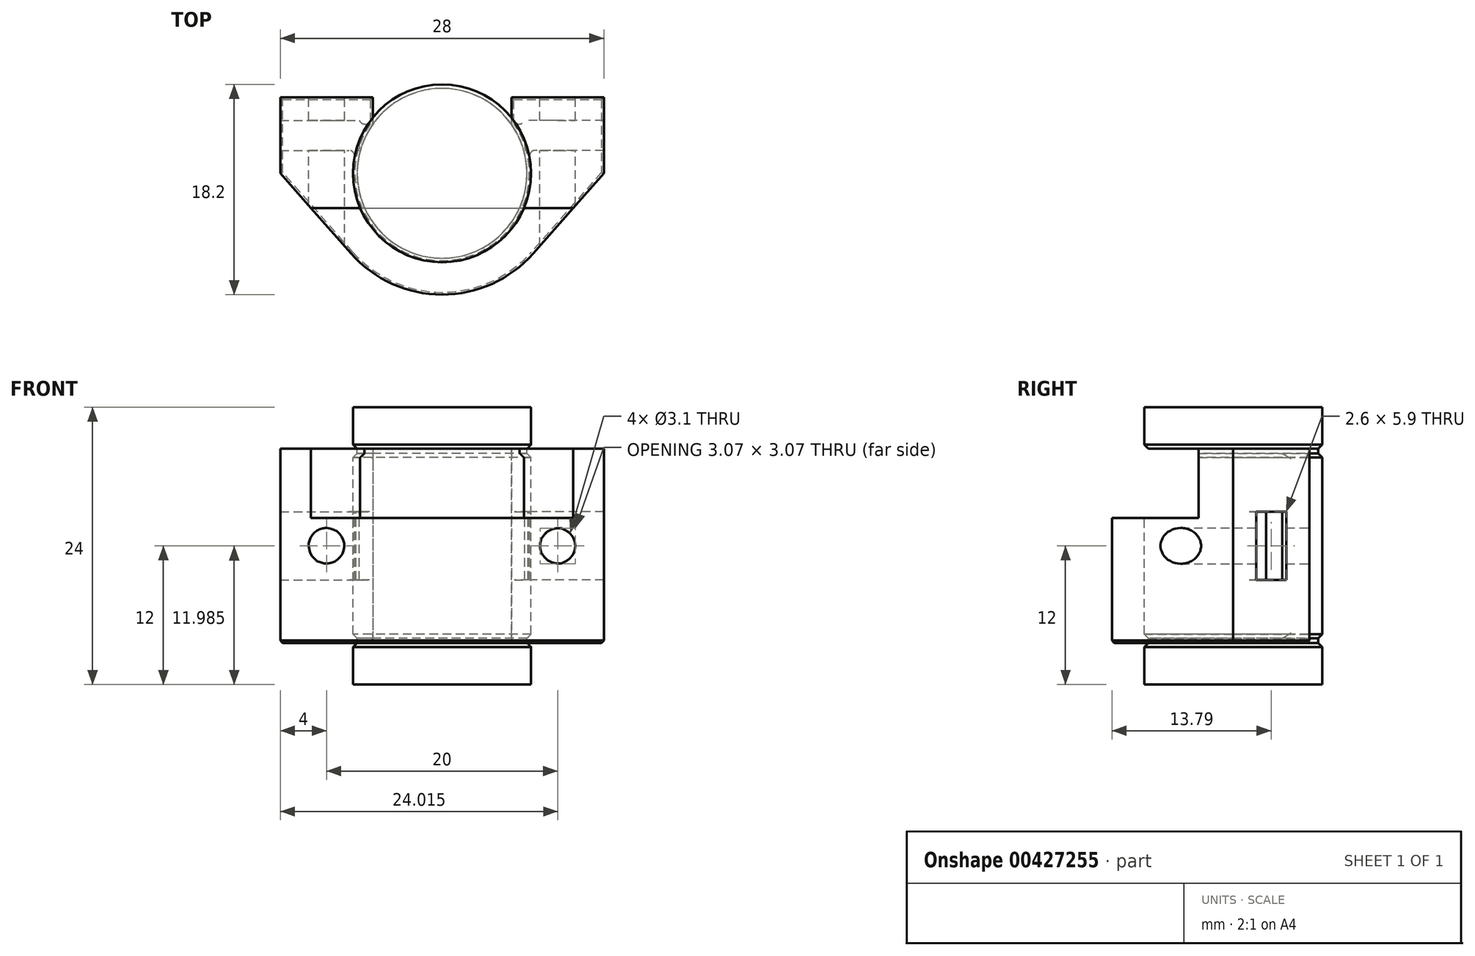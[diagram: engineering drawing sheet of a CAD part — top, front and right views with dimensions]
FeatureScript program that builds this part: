
annotation { "Feature Type Name" : "Feature", "Feature Type Description" : "" }
export const myFeature = defineFeature(function(context is Context, id is Id, definition is map)
    precondition{}
    {
        {
            var Q0;
            Q0=qCreatedBy(makeId("Front.planeOp"),FACE);
            var sketch = newSketch(context, id + "F0", { "sketchPlane" : qUnion([Q0])});
            skLineSegment(sketch, "E0", {"start": v(0, 12) * mm, "end": v(0, -12) * mm});
            skLineSegment(sketch, "E1.bottom", {"start": v(-4, 12) * mm, "end": v(-7.5, 12) * mm});
            skLineSegment(sketch, "E1.top", {"start": v(-4, -12) * mm, "end": v(-7.5, -12) * mm});
            skLineSegment(sketch, "E1.left", {"start": v(-4, 12) * mm, "end": v(-4, -12) * mm, "construction": true});
            skLineSegment(sketch, "E2", {"start": v(-7.5, 12) * mm, "end": v(-7.5, 8.75) * mm, "construction": true});
            skLineSegment(sketch, "E3", {"start": v(-7.5, 8.75) * mm, "end": v(-7.15, 8.75) * mm, "construction": true});
            skLineSegment(sketch, "E4", {"start": v(-7.15, 8.75) * mm, "end": v(-7.15, 7.65) * mm, "construction": true});
            skLineSegment(sketch, "E5", {"start": v(-7.15, 7.65) * mm, "end": v(-7.5, 7.65) * mm, "construction": true});
            skLineSegment(sketch, "E6", {"start": v(-7.5, 7.65) * mm, "end": v(-7.5, 0) * mm, "construction": true});
            skLineSegment(sketch, "E7.MirrorCS", {"start": v(-7.5, -8.75) * mm, "end": v(-7.15, -8.75) * mm, "construction": true});
            skLineSegment(sketch, "E8.MirrorCS", {"start": v(-7.15, -8.75) * mm, "end": v(-7.15, -7.65) * mm, "construction": true});
            skLineSegment(sketch, "E9.MirrorCS", {"start": v(-7.15, -7.65) * mm, "end": v(-7.5, -7.65) * mm, "construction": true});
            skLineSegment(sketch, "E10", {"start": v(-7.5, 0) * mm, "end": v(-7.5, -7.65) * mm, "construction": true});
            skLineSegment(sketch, "E11", {"start": v(-7.5, -8.75) * mm, "end": v(-7.5, -12) * mm, "construction": true});
            skLineSegment(sketch, "E12.0", {"start": v(-7.7, 12) * mm, "end": v(-7.7, 8.75) * mm});
            skLineSegment(sketch, "E13.0", {"start": v(-7.35, 8.75) * mm, "end": v(-7.35, 7.65) * mm});
            skLineSegment(sketch, "E14", {"start": v(-7.7, 8.75) * mm, "end": v(-7.35, 8.4) * mm});
            skLineSegment(sketch, "E15", {"start": v(-7.7, 7.65) * mm, "end": v(-7.7, 0) * mm});
            skLineSegment(sketch, "E16", {"start": v(-7.7, 7.65) * mm, "end": v(-7.35, 8) * mm});
            skLineSegment(sketch, "E17", {"start": v(-7.7, 12) * mm, "end": v(-7.5, 12) * mm});
            skLineSegment(sketch, "E18.MirrorCS", {"start": v(-7.7, -7.65) * mm, "end": v(-7.7, 0) * mm});
            skLineSegment(sketch, "E19.MirrorCS", {"start": v(-7.7, -7.65) * mm, "end": v(-7.35, -8) * mm});
            skLineSegment(sketch, "E20.MirrorCS", {"start": v(-7.35, -8.75) * mm, "end": v(-7.35, -7.65) * mm});
            skLineSegment(sketch, "E21.MirrorCS", {"start": v(-7.7, -8.75) * mm, "end": v(-7.35, -8.4) * mm});
            skLineSegment(sketch, "E22.MirrorCS", {"start": v(-7.7, -12) * mm, "end": v(-7.7, -8.75) * mm});
            skLineSegment(sketch, "E23.MirrorCS", {"start": v(-7.7, -12) * mm, "end": v(-7.5, -12) * mm});
            skLineSegment(sketch, "E24", {"start": v(-4, 12) * mm, "end": v(0, 12) * mm});
            skLineSegment(sketch, "E25", {"start": v(-4, -12) * mm, "end": v(0, -12) * mm});
            skSolve(sketch);
        }
        {
            var Q0;
            Q0=qCreatedBy(makeId("Top.planeOp"),FACE);
            var sketch = newSketch(context, id + "F1", { "sketchPlane" : qUnion([Q0])});
            skLineSegment(sketch, "E26", {"start": v(-5, 6.6) * mm, "end": v(5, 6.6) * mm, "construction": true});
            skCircle(sketch, "E27", {"center": v(0, 0) * mm, "radius": 7.5 * mm, "construction": true});
            skLineSegment(sketch, "E28", {"start": v(5, 6.6) * mm, "end": v(5, 5.6) * mm, "construction": true});
            skLineSegment(sketch, "E29", {"start": v(-5, 6.6) * mm, "end": v(-5, 5.6) * mm, "construction": true});
            skLineSegment(sketch, "E30", {"start": v(-5, 6.6) * mm, "end": v(-10, 6.6) * mm, "construction": true});
            skLineSegment(sketch, "E31", {"start": v(5, 6.6) * mm, "end": v(10, 6.6) * mm, "construction": true});
            skLineSegment(sketch, "E32", {"start": v(-10, 6.6) * mm, "end": v(-10, 4.6) * mm, "construction": true});
            skLineSegment(sketch, "E33.bottom", {"start": v(-12.85, 4.6) * mm, "end": v(-7.15, 4.6) * mm, "construction": true});
            skLineSegment(sketch, "E33.top", {"start": v(-12.85, 2) * mm, "end": v(-7.15, 2) * mm, "construction": true});
            skLineSegment(sketch, "E33.left", {"start": v(-12.85, 4.6) * mm, "end": v(-12.85, 2) * mm, "construction": true});
            skLineSegment(sketch, "E33.right", {"start": v(-7.15, 4.6) * mm, "end": v(-7.15, 2) * mm, "construction": true});
            skSolve(sketch);
        }
        {
            var Q0;
            Q0=qSketchRegion(id+"F0",true);
            var Q1;
            Q1=sQuery(id+"F0.wireOp",EDGE,"E0");
            revolve(context, id + "F2", {"entities" : qUnion([Q0]), "axis" : qUnion([Q1]), "revolveType" : RevolveType.FULL});
        }
        {
            var Q0;
            Q0=qCreatedBy(makeId("Top.planeOp"),FACE);
            var sketch = newSketch(context, id + "F3", { "sketchPlane" : qUnion([Q0])});
            skPoint(sketch, "E34.0", {"position": v(0, 6.6) * mm});
            skLineSegment(sketch, "E35", {"start": v(0, 6.6) * mm, "end": v(-14, 6.6) * mm, "construction": true});
            skLineSegment(sketch, "E36", {"start": v(-14, 6.6) * mm, "end": v(-14, 0) * mm});
            skLineSegment(sketch, "E37.MirrorCS", {"start": v(0, 6.6) * mm, "end": v(14, 6.6) * mm, "construction": true});
            skLineSegment(sketch, "E38.MirrorCS", {"start": v(14, 6.6) * mm, "end": v(14, 0) * mm});
            skCircle(sketch, "E39.0", {"center": v(0, 0) * mm, "radius": 7.5 * mm, "construction": true});
            skCircle(sketch, "E40.0", {"center": v(0, 0) * mm, "radius": 10.5 * mm, "construction": true});
            skArc(sketch, "E41", {"start": v(-7.88, -6.95) * mm, "mid": v(0, -10.5) * mm, "end": v(7.88, -6.95) * mm});
            skLineSegment(sketch, "E42", {"start": v(-14, 0) * mm, "end": v(-7.87, -6.95) * mm});
            skLineSegment(sketch, "E43.MirrorCS", {"start": v(14, 0) * mm, "end": v(7.87, -6.95) * mm});
            skLineSegment(sketch, "E44.0", {"start": v(-12.85, 4.6) * mm, "end": v(-7.15, 4.6) * mm, "construction": true});
            skLineSegment(sketch, "E45.0", {"start": v(-12.85, 2) * mm, "end": v(-7.15, 2) * mm, "construction": true});
            skLineSegment(sketch, "E46.0", {"start": v(-12.85, 4.6) * mm, "end": v(-12.85, 2) * mm, "construction": true});
            skLineSegment(sketch, "E47", {"start": v(-14, 6.6) * mm, "end": v(-6, 6.6) * mm});
            skLineSegment(sketch, "E48.MirrorCS", {"start": v(14, 6.6) * mm, "end": v(6, 6.6) * mm});
            skLineSegment(sketch, "E49.0", {"start": v(-7.15, 4.6) * mm, "end": v(-7.15, 2) * mm, "construction": true});
            skLineSegment(sketch, "E50", {"start": v(-6, 6.6) * mm, "end": v(-6, 3.3) * mm});
            skPoint(sketch, "E50.endSnap0", {"position": v(-7.15, 3.3) * mm});
            skLineSegment(sketch, "E51", {"start": v(-6, 3.3) * mm, "end": v(0, 3.3) * mm});
            skLineSegment(sketch, "E52.MirrorCS", {"start": v(6, 6.6) * mm, "end": v(6, 3.3) * mm});
            skLineSegment(sketch, "E53.MirrorCS", {"start": v(6, 3.3) * mm, "end": v(0, 3.3) * mm});
            skSolve(sketch);
        }
        {
            var Q0;
            Q0=qSketchRegion(id+"F3",true);
            var Q1;
            Q1=sQuery(id+"F0.wireOp",VERTEX,"E14.end");
            var Q2;
            Q2=sQuery(id+"F0.wireOp",VERTEX,"E21.MirrorCS.end");
            extrude(context, id + "F4", {"entities" : qUnion([Q0]), "endBound" : BoundingType.UP_TO_VERTEX, "endBoundEntityVertex" : qUnion([Q1]), "depth" : 25 * mm, "hasSecondDirection" : true, "secondDirectionBound" : SecondDirectionBoundingType.UP_TO_VERTEX, "secondDirectionOppositeDirection" : true, "secondDirectionBoundEntityVertex" : qUnion([Q2]), "secondDirectionDepth" : 25 * mm});
        }
        {
            var Q0;
            Q0=makeQuery(id+"F4.opExtrude","SWEPT_FACE",FACE,{"disambiguationData":[OSD([sQuery(id+"F3.wireOp",EDGE,"E48.MirrorCS")])]});
            var sketch = newSketch(context, id + "F5", { "sketchPlane" : qUnion([Q0])});
            skPoint(sketch, "E54.0", {"position": v(-10, 0) * mm});
            skPoint(sketch, "E55.0", {"position": v(10, 0) * mm});
            skSolve(sketch);
        }
        {
            var Q0;
            Q0=makeQuery(id+"F2.opRevolve","SWEPT_BODY",BODY,{"disambiguationData":[OSD([sQuery(id+"F0.wireOp",EDGE,"E0"),sQuery(id+"F0.wireOp",EDGE,"E1.bottom"),sQuery(id+"F0.wireOp",EDGE,"E1.top"),sQuery(id+"F0.wireOp",EDGE,"E12.0"),sQuery(id+"F0.wireOp",EDGE,"E13.0"),sQuery(id+"F0.wireOp",EDGE,"E14"),sQuery(id+"F0.wireOp",EDGE,"E15"),sQuery(id+"F0.wireOp",EDGE,"E16"),sQuery(id+"F0.wireOp",EDGE,"E17"),sQuery(id+"F0.wireOp",EDGE,"E18.MirrorCS"),sQuery(id+"F0.wireOp",EDGE,"E19.MirrorCS"),sQuery(id+"F0.wireOp",EDGE,"E20.MirrorCS"),sQuery(id+"F0.wireOp",EDGE,"E21.MirrorCS"),sQuery(id+"F0.wireOp",EDGE,"E22.MirrorCS"),sQuery(id+"F0.wireOp",EDGE,"E23.MirrorCS"),sQuery(id+"F0.wireOp",EDGE,"E24"),sQuery(id+"F0.wireOp",EDGE,"E25")])]});
            var Q1;
            Q1=makeQuery(id+"F4.opExtrude","SWEPT_BODY",BODY,{"disambiguationData":[OSD([sQuery(id+"F3.wireOp",EDGE,"E36"),sQuery(id+"F3.wireOp",EDGE,"E38.MirrorCS"),sQuery(id+"F3.wireOp",EDGE,"E41"),sQuery(id+"F3.wireOp",EDGE,"E42"),sQuery(id+"F3.wireOp",EDGE,"E43.MirrorCS"),sQuery(id+"F3.wireOp",EDGE,"E47"),sQuery(id+"F3.wireOp",EDGE,"E48.MirrorCS"),sQuery(id+"F3.wireOp",EDGE,"E50"),sQuery(id+"F3.wireOp",EDGE,"E51"),sQuery(id+"F3.wireOp",EDGE,"E52.MirrorCS"),sQuery(id+"F3.wireOp",EDGE,"E53.MirrorCS")])]});
            booleanBodies(context, id + "F6", {"operationType" : BooleanOperationType.SUBTRACTION, "tools" : qUnion([Q0]), "targets" : qUnion([Q1]), "keepTools" : true});
        }
        {
            var Q0;
            Q0=sQuery(id+"F5.wireOp",VERTEX,"E54.0");
            var Q1;
            Q1=sQuery(id+"F5.wireOp",VERTEX,"E55.0");
            var Q2;
            Q2=makeQuery(id+"F4.opExtrude","SWEPT_BODY",BODY,{"disambiguationData":[OSD([sQuery(id+"F3.wireOp",EDGE,"E36"),sQuery(id+"F3.wireOp",EDGE,"E38.MirrorCS"),sQuery(id+"F3.wireOp",EDGE,"E41"),sQuery(id+"F3.wireOp",EDGE,"E42"),sQuery(id+"F3.wireOp",EDGE,"E43.MirrorCS"),sQuery(id+"F3.wireOp",EDGE,"E47"),sQuery(id+"F3.wireOp",EDGE,"E48.MirrorCS"),sQuery(id+"F3.wireOp",EDGE,"E50"),sQuery(id+"F3.wireOp",EDGE,"E51"),sQuery(id+"F3.wireOp",EDGE,"E52.MirrorCS"),sQuery(id+"F3.wireOp",EDGE,"E53.MirrorCS")])]});
            hole(context, id + "F7", {"style" : HoleStyle.SIMPLE, "endStyle" : HoleEndStyle.THROUGH, "holeDiameter" : 3.1 * mm, "isTappedThrough" : true, "tappedDepth" : 12 * mm, "tapClearance" : 3, "locations" : qUnion([Q0, Q1]), "scope" : qUnion([Q2])});
        }
        {
            var Q0;
            Q0=qCreatedBy(makeId("Top.planeOp"),FACE);
            var sketch = newSketch(context, id + "F8", { "sketchPlane" : qUnion([Q0])});
            skLineSegment(sketch, "E56.0", {"start": v(-12.85, 2) * mm, "end": v(-7.15, 2) * mm});
            skLineSegment(sketch, "E57.0", {"start": v(-12.85, 4.6) * mm, "end": v(-12.85, 2) * mm, "construction": true});
            skLineSegment(sketch, "E58.0", {"start": v(-12.85, 4.6) * mm, "end": v(-7.15, 4.6) * mm});
            skLineSegment(sketch, "E59.0", {"start": v(-7.15, 4.6) * mm, "end": v(-7.15, 2) * mm});
            skLineSegment(sketch, "E60.MirrorCS", {"start": v(12.85, 4.6) * mm, "end": v(7.15, 4.6) * mm});
            skLineSegment(sketch, "E61.MirrorCS", {"start": v(12.85, 4.6) * mm, "end": v(12.85, 2) * mm, "construction": true});
            skLineSegment(sketch, "E62.MirrorCS", {"start": v(12.85, 2) * mm, "end": v(7.15, 2) * mm});
            skLineSegment(sketch, "E63.MirrorCS", {"start": v(7.15, 4.6) * mm, "end": v(7.15, 2) * mm});
            skLineSegment(sketch, "E64", {"start": v(-12.85, 4.6) * mm, "end": v(-19.02, 4.6) * mm});
            skLineSegment(sketch, "E65", {"start": v(-19.02, 4.6) * mm, "end": v(-19.02, 2) * mm});
            skLineSegment(sketch, "E66", {"start": v(-19.02, 2) * mm, "end": v(-12.85, 2) * mm});
            skLineSegment(sketch, "E67.MirrorCS", {"start": v(12.85, 4.6) * mm, "end": v(19.02, 4.6) * mm});
            skLineSegment(sketch, "E68.MirrorCS", {"start": v(19.02, 4.6) * mm, "end": v(19.02, 2) * mm});
            skLineSegment(sketch, "E69.MirrorCS", {"start": v(19.02, 2) * mm, "end": v(12.85, 2) * mm});
            skSolve(sketch);
        }
        {
            var Q0;
            Q0=qSketchRegion(id+"F8",true);
            extrude(context, id + "F9", {"entities" : qUnion([Q0]), "operationType" : NewBodyOperationType.REMOVE, "endBound" : BoundingType.SYMMETRIC, "depth" : (0.4 + 5.5) * mm});
        }
        {
            var Q0;
            Q0=makeQuery(id+"F4.opExtrude","TWEAK_EDGE",EDGE,{"derivedFrom":[makeQuery(id+"F3.imprint","IMPRINT",EDGE,{"derivedFrom":sQuery(id+"F3.wireOp",EDGE,"E47")}),makeQuery(id+"F3.imprint","IMPRINT",EDGE,{"derivedFrom":sQuery(id+"F3.wireOp",EDGE,"E50")})]});
            var Q1;
            Q1=makeQuery(id+"F4.opExtrude","TWEAK_EDGE",EDGE,{"derivedFrom":[makeQuery(id+"F3.imprint","IMPRINT",EDGE,{"derivedFrom":sQuery(id+"F3.wireOp",EDGE,"E36")}),makeQuery(id+"F3.imprint","IMPRINT",EDGE,{"derivedFrom":sQuery(id+"F3.wireOp",EDGE,"E47")})]});
            var Q2;
            Q2=makeQuery(id+"F4.opExtrude","TWEAK_EDGE",EDGE,{"derivedFrom":[makeQuery(id+"F3.imprint","IMPRINT",EDGE,{"derivedFrom":sQuery(id+"F3.wireOp",EDGE,"E48.MirrorCS")}),makeQuery(id+"F3.imprint","IMPRINT",EDGE,{"derivedFrom":sQuery(id+"F3.wireOp",EDGE,"E52.MirrorCS")})]});
            var Q3;
            Q3=makeQuery(id+"F4.opExtrude","TWEAK_EDGE",EDGE,{"derivedFrom":[makeQuery(id+"F3.imprint","IMPRINT",EDGE,{"derivedFrom":sQuery(id+"F3.wireOp",EDGE,"E38.MirrorCS")}),makeQuery(id+"F3.imprint","IMPRINT",EDGE,{"derivedFrom":sQuery(id+"F3.wireOp",EDGE,"E48.MirrorCS")})]});
            var Q4;
            Q4=makeQuery(id+"F6.opBoolean","INTERSECT",EDGE,{"derivedFrom":[makeQuery(id+"F2.opRevolve","SWEPT_FACE",FACE,{"disambiguationData":[OSD([sQuery(id+"F0.wireOp",EDGE,"E15"),sQuery(id+"F0.wireOp",EDGE,"E18.MirrorCS")])]}),makeQuery(id+"F4.opExtrude","SWEPT_FACE",FACE,{"disambiguationData":[OSD([sQuery(id+"F3.wireOp",EDGE,"E52.MirrorCS")])]})]});
            var Q5;
            Q5=makeQuery(id+"F6.opBoolean","INTERSECT",EDGE,{"derivedFrom":[makeQuery(id+"F2.opRevolve","SWEPT_FACE",FACE,{"disambiguationData":[OSD([sQuery(id+"F0.wireOp",EDGE,"E15"),sQuery(id+"F0.wireOp",EDGE,"E18.MirrorCS")])]}),makeQuery(id+"F4.opExtrude","SWEPT_FACE",FACE,{"disambiguationData":[OSD([sQuery(id+"F3.wireOp",EDGE,"E50")])]})]});
            var Q6;
            Q6=makeQuery(id+"F6.opBoolean","INTERSECT",EDGE,{"derivedFrom":[makeQuery(id+"F2.opRevolve","SWEPT_FACE",FACE,{"disambiguationData":[OSD([sQuery(id+"F0.wireOp",EDGE,"E13.0")])]}),makeQuery(id+"F4.opExtrude","SWEPT_FACE",FACE,{"disambiguationData":[OSD([sQuery(id+"F3.wireOp",EDGE,"E50")])]})]});
            var Q7;
            Q7=makeQuery(id+"F6.opBoolean","INTERSECT",EDGE,{"derivedFrom":[makeQuery(id+"F2.opRevolve","SWEPT_FACE",FACE,{"disambiguationData":[OSD([sQuery(id+"F0.wireOp",EDGE,"E20.MirrorCS")])]}),makeQuery(id+"F4.opExtrude","SWEPT_FACE",FACE,{"disambiguationData":[OSD([sQuery(id+"F3.wireOp",EDGE,"E50")])]})]});
            var Q8;
            Q8=makeQuery(id+"F6.opBoolean","INTERSECT",EDGE,{"derivedFrom":[makeQuery(id+"F2.opRevolve","SWEPT_FACE",FACE,{"disambiguationData":[OSD([sQuery(id+"F0.wireOp",EDGE,"E13.0")])]}),makeQuery(id+"F4.opExtrude","SWEPT_FACE",FACE,{"disambiguationData":[OSD([sQuery(id+"F3.wireOp",EDGE,"E52.MirrorCS")])]})]});
            var Q9;
            Q9=makeQuery(id+"F6.opBoolean","INTERSECT",EDGE,{"derivedFrom":[makeQuery(id+"F2.opRevolve","SWEPT_FACE",FACE,{"disambiguationData":[OSD([sQuery(id+"F0.wireOp",EDGE,"E20.MirrorCS")])]}),makeQuery(id+"F4.opExtrude","SWEPT_FACE",FACE,{"disambiguationData":[OSD([sQuery(id+"F3.wireOp",EDGE,"E52.MirrorCS")])]})]});
            var Q10;
            Q10=makeQuery(id+"F4.opExtrude","TWEAK_EDGE",EDGE,{"derivedFrom":[makeQuery(id+"F3.imprint","IMPRINT",EDGE,{"derivedFrom":sQuery(id+"F3.wireOp",EDGE,"E36")}),makeQuery(id+"F3.imprint","IMPRINT",EDGE,{"derivedFrom":sQuery(id+"F3.wireOp",EDGE,"E42")})]});
            var Q11;
            Q11=makeQuery(id+"F4.opExtrude","TWEAK_EDGE",EDGE,{"derivedFrom":[makeQuery(id+"F3.imprint","IMPRINT",EDGE,{"derivedFrom":sQuery(id+"F3.wireOp",EDGE,"E38.MirrorCS")}),makeQuery(id+"F3.imprint","IMPRINT",EDGE,{"derivedFrom":sQuery(id+"F3.wireOp",EDGE,"E43.MirrorCS")})]});
            var Q12;
            Q12=makeQuery(id+"F9.boolean.opBoolean","INTERSECT",EDGE,{"derivedFrom":[makeQuery(id+"F6.opBoolean","COPY",FACE,{"derivedFrom":makeQuery(id+"F2.opRevolve","SWEPT_FACE",FACE,{"disambiguationData":[OSD([sQuery(id+"F0.wireOp",EDGE,"E15"),sQuery(id+"F0.wireOp",EDGE,"E18.MirrorCS")])]})}),makeQuery(id+"F9.opExtrude","SWEPT_FACE",FACE,{"disambiguationData":[OSD([sQuery(id+"F8.wireOp",EDGE,"E59.0")])]})]});
            var Q13;
            Q13=makeQuery(id+"F9.boolean.opBoolean","INTERSECT",EDGE,{"derivedFrom":[makeQuery(id+"F6.opBoolean","COPY",FACE,{"derivedFrom":makeQuery(id+"F2.opRevolve","SWEPT_FACE",FACE,{"disambiguationData":[OSD([sQuery(id+"F0.wireOp",EDGE,"E15"),sQuery(id+"F0.wireOp",EDGE,"E18.MirrorCS")])]})}),makeQuery(id+"F9.opExtrude","SWEPT_FACE",FACE,{"disambiguationData":[OSD([sQuery(id+"F8.wireOp",EDGE,"E63.MirrorCS")])]})]});
            var Q14;
            Q14=makeQuery(id+"F9.boolean.opBoolean","INTERSECT",EDGE,{"derivedFrom":[makeQuery(id+"F6.opBoolean","COPY",FACE,{"derivedFrom":makeQuery(id+"F2.opRevolve","SWEPT_FACE",FACE,{"disambiguationData":[OSD([sQuery(id+"F0.wireOp",EDGE,"E15"),sQuery(id+"F0.wireOp",EDGE,"E18.MirrorCS")])]})}),makeQuery(id+"F9.opExtrude","SWEPT_FACE",FACE,{"disambiguationData":[OSD([sQuery(id+"F8.wireOp",EDGE,"E56.0"),sQuery(id+"F8.wireOp",EDGE,"E66")])]})]});
            var Q15;
            Q15=makeQuery(id+"F9.boolean.opBoolean","INTERSECT",EDGE,{"derivedFrom":[makeQuery(id+"F6.opBoolean","COPY",FACE,{"derivedFrom":makeQuery(id+"F2.opRevolve","SWEPT_FACE",FACE,{"disambiguationData":[OSD([sQuery(id+"F0.wireOp",EDGE,"E15"),sQuery(id+"F0.wireOp",EDGE,"E18.MirrorCS")])]})}),makeQuery(id+"F9.opExtrude","SWEPT_FACE",FACE,{"disambiguationData":[OSD([sQuery(id+"F8.wireOp",EDGE,"E62.MirrorCS"),sQuery(id+"F8.wireOp",EDGE,"E69.MirrorCS")])]})]});
            fillet(context, id + "F10", {"entities" : qUnion([Q0, Q1, Q2, Q3, Q4, Q5, Q6, Q7, Q8, Q9, Q10, Q11, Q12, Q13, Q14, Q15]), "radius" : .5 * mm, "allowEdgeOverflow" : false});
        }
        {
            var Q0;
            Q0=makeQuery(id+"F4.opExtrude","CAP_FACE",FACE,{"disambiguationData":[OSD([sQuery(id+"F3.wireOp",EDGE,"E36"),sQuery(id+"F3.wireOp",EDGE,"E38.MirrorCS"),sQuery(id+"F3.wireOp",EDGE,"E41"),sQuery(id+"F3.wireOp",EDGE,"E42"),sQuery(id+"F3.wireOp",EDGE,"E43.MirrorCS"),sQuery(id+"F3.wireOp",EDGE,"E47"),sQuery(id+"F3.wireOp",EDGE,"E48.MirrorCS"),sQuery(id+"F3.wireOp",EDGE,"E50"),sQuery(id+"F3.wireOp",EDGE,"E51"),sQuery(id+"F3.wireOp",EDGE,"E52.MirrorCS"),sQuery(id+"F3.wireOp",EDGE,"E53.MirrorCS")])],"isStart":true});
            chamfer(context, id + "F11", {"entities" : qUnion([Q0]), "width" : .2 * mm});
        }
        {
            var Q0;
            Q0=makeQuery(id+"F4.opExtrude","CAP_FACE",FACE,{"disambiguationData":[OSD([sQuery(id+"F3.wireOp",EDGE,"E36"),sQuery(id+"F3.wireOp",EDGE,"E38.MirrorCS"),sQuery(id+"F3.wireOp",EDGE,"E41"),sQuery(id+"F3.wireOp",EDGE,"E42"),sQuery(id+"F3.wireOp",EDGE,"E43.MirrorCS"),sQuery(id+"F3.wireOp",EDGE,"E47"),sQuery(id+"F3.wireOp",EDGE,"E48.MirrorCS"),sQuery(id+"F3.wireOp",EDGE,"E50"),sQuery(id+"F3.wireOp",EDGE,"E51"),sQuery(id+"F3.wireOp",EDGE,"E52.MirrorCS"),sQuery(id+"F3.wireOp",EDGE,"E53.MirrorCS")])],"isStart":false});
            var sketch = newSketch(context, id + "F12", { "sketchPlane" : qUnion([Q0])});
            skCircle(sketch, "E70.0", {"center": v(0, 0) * mm, "radius": 7.5 * mm, "construction": true});
            skLineSegment(sketch, "E71", {"start": v(0, -7.5) * mm, "end": v(0, -3) * mm, "construction": true});
            skLineSegment(sketch, "E72.bottom", {"start": v(-29.21, -15.23) * mm, "end": v(29.21, -15.23) * mm});
            skLineSegment(sketch, "E72.top", {"start": v(-29.21, -3) * mm, "end": v(29.21, -3) * mm});
            skLineSegment(sketch, "E72.left", {"start": v(-29.21, -15.23) * mm, "end": v(-29.21, -3) * mm});
            skLineSegment(sketch, "E72.right", {"start": v(29.21, -15.23) * mm, "end": v(29.21, -3) * mm});
            skSolve(sketch);
        }
        {
            var Q0;
            Q0=qSketchRegion(id+"F12",true);
            extrude(context, id + "F13", {"entities" : qUnion([Q0]), "operationType" : NewBodyOperationType.REMOVE, "oppositeDirection" : true, "depth" : 6 * mm});
        }
    });
